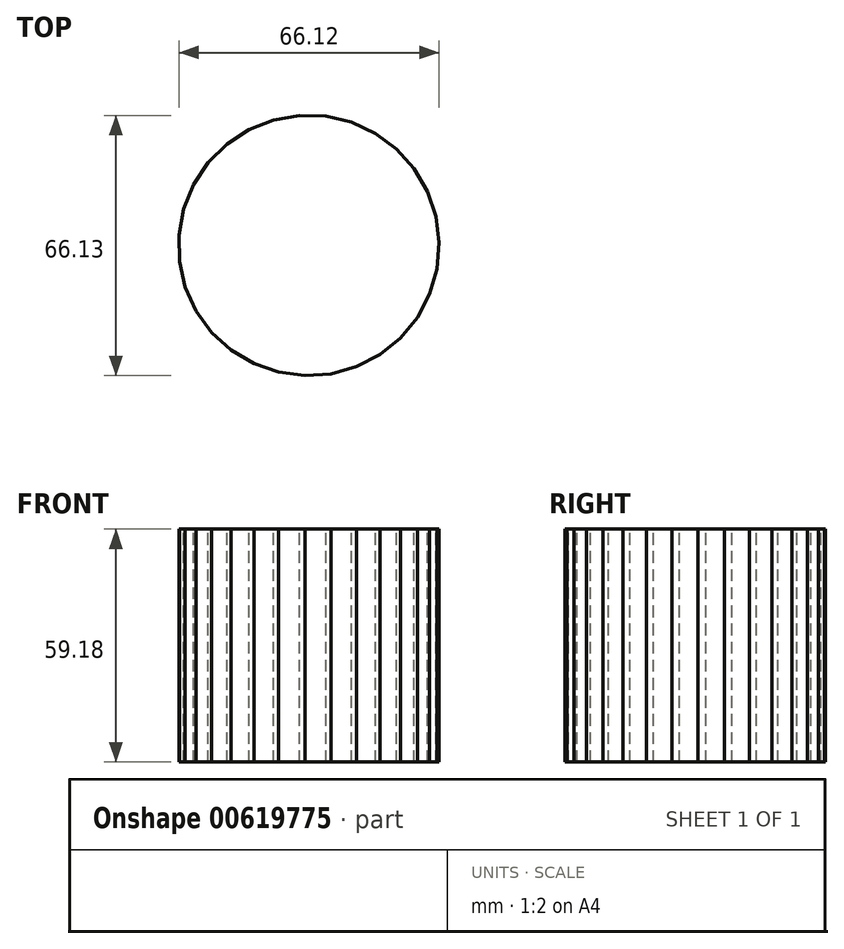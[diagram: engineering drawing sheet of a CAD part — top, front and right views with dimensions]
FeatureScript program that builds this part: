
annotation { "Feature Type Name" : "Feature", "Feature Type Description" : "" }
export const myFeature = defineFeature(function(context is Context, id is Id, definition is map)
    precondition{}
    {
        {
            var Q0;
            Q0=qCreatedBy(makeId("Top.planeOp"),FACE);
            var sketch = newSketch(context, id + "F0", { "sketchPlane" : qUnion([Q0])});
            skCircle(sketch, "E0.cCircle", {"center": v(0, 0) * mm, "radius": 32.95 * mm, "construction": true});
            skLineSegment(sketch, "E0.0", {"start": v(23.32, -23.52) * mm, "end": v(18.1, -27.73) * mm});
            skLineSegment(sketch, "E0.1", {"start": v(18.1, -27.73) * mm, "end": v(12.15, -30.8) * mm});
            skLineSegment(sketch, "E0.2", {"start": v(12.15, -30.8) * mm, "end": v(5.7, -32.62) * mm});
            skLineSegment(sketch, "E0.3", {"start": v(5.7, -32.62) * mm, "end": v(-0.98, -33.1) * mm});
            skLineSegment(sketch, "E0.4", {"start": v(-0.98, -33.1) * mm, "end": v(-7.62, -32.23) * mm});
            skLineSegment(sketch, "E0.5", {"start": v(-7.62, -32.23) * mm, "end": v(-13.95, -30.03) * mm});
            skLineSegment(sketch, "E0.6", {"start": v(-13.95, -30.03) * mm, "end": v(-19.71, -26.6) * mm});
            skLineSegment(sketch, "E0.7", {"start": v(-19.71, -26.6) * mm, "end": v(-24.67, -22.1) * mm});
            skLineSegment(sketch, "E0.8", {"start": v(-24.67, -22.1) * mm, "end": v(-28.6, -16.68) * mm});
            skLineSegment(sketch, "E0.9", {"start": v(-28.6, -16.68) * mm, "end": v(-31.38, -10.58) * mm});
            skLineSegment(sketch, "E0.10", {"start": v(-31.38, -10.58) * mm, "end": v(-32.87, -4.05) * mm});
            skLineSegment(sketch, "E0.11", {"start": v(-32.87, -4.05) * mm, "end": v(-33, 2.65) * mm});
            skLineSegment(sketch, "E0.12", {"start": v(-33, 2.65) * mm, "end": v(-31.8, 9.24) * mm});
            skLineSegment(sketch, "E0.13", {"start": v(-31.8, 9.24) * mm, "end": v(-29.29, 15.46) * mm});
            skLineSegment(sketch, "E0.14", {"start": v(-29.29, 15.46) * mm, "end": v(-25.58, 21.04) * mm});
            skLineSegment(sketch, "E0.15", {"start": v(-25.58, 21.04) * mm, "end": v(-20.82, 25.75) * mm});
            skLineSegment(sketch, "E0.16", {"start": v(-20.82, 25.75) * mm, "end": v(-15.2, 29.42) * mm});
            skLineSegment(sketch, "E0.17", {"start": v(-15.2, 29.42) * mm, "end": v(-8.98, 31.88) * mm});
            skLineSegment(sketch, "E0.18", {"start": v(-8.98, 31.88) * mm, "end": v(-2.38, 33.03) * mm});
            skLineSegment(sketch, "E0.19", {"start": v(-2.38, 33.03) * mm, "end": v(4.32, 32.83) * mm});
            skLineSegment(sketch, "E0.20", {"start": v(4.32, 32.83) * mm, "end": v(10.84, 31.3) * mm});
            skLineSegment(sketch, "E0.21", {"start": v(10.84, 31.3) * mm, "end": v(16.92, 28.47) * mm});
            skLineSegment(sketch, "E0.22", {"start": v(16.92, 28.47) * mm, "end": v(22.3, 24.48) * mm});
            skLineSegment(sketch, "E0.23", {"start": v(22.3, 24.48) * mm, "end": v(26.77, 19.49) * mm});
            skLineSegment(sketch, "E0.24", {"start": v(26.77, 19.49) * mm, "end": v(30.15, 13.7) * mm});
            skLineSegment(sketch, "E0.25", {"start": v(30.15, 13.7) * mm, "end": v(32.3, 7.35) * mm});
            skLineSegment(sketch, "E0.26", {"start": v(32.3, 7.35) * mm, "end": v(33.1, 0.7) * mm});
            skLineSegment(sketch, "E0.27", {"start": v(33.1, 0.7) * mm, "end": v(32.57, -5.98) * mm});
            skLineSegment(sketch, "E0.28", {"start": v(32.57, -5.98) * mm, "end": v(30.7, -12.41) * mm});
            skLineSegment(sketch, "E0.29", {"start": v(30.7, -12.41) * mm, "end": v(27.57, -18.34) * mm});
            skLineSegment(sketch, "E0.30", {"start": v(27.57, -18.34) * mm, "end": v(23.32, -23.52) * mm});
            skPoint(sketch, "E0.0.midPoint", {"position": v(20.71, -25.62) * mm});
            skSolve(sketch);
        }
        {
            var Q0;
            Q0=makeQuery(id+"F0.imprint","IMPRINT",FACE,{"disambiguationData":[TD([[makeQuery(id+"F0.imprint","IMPRINT",EDGE,{"derivedFrom":sQuery(id+"F0.wireOp",EDGE,"E0.0")}),-1.0]])]});
            extrude(context, id + "F1", {"entities" : qUnion([Q0]), "oppositeDirection" : true, "depth" : 33.78 * mm, "offsetDistance" : 25.4 * mm, "hasSecondDirection" : true, "secondDirectionOppositeDirection" : false, "secondDirectionDepth" : 25.4 * mm});
        }
    });
